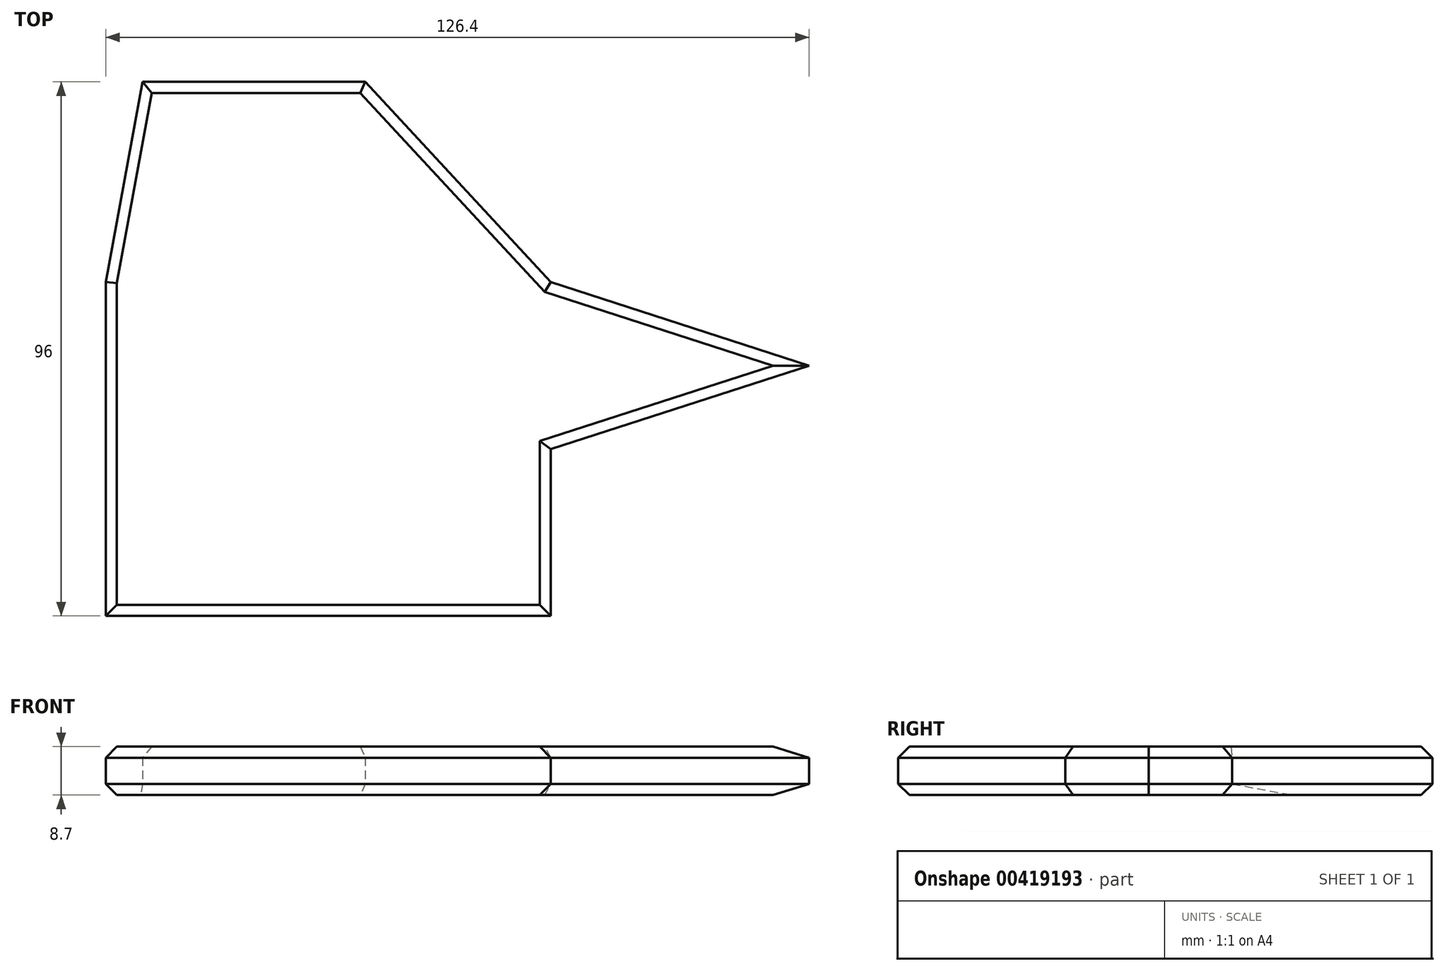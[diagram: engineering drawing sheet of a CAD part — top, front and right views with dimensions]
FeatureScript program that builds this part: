
annotation { "Feature Type Name" : "Feature", "Feature Type Description" : "" }
export const myFeature = defineFeature(function(context is Context, id is Id, definition is map)
    precondition{}
    {
        {
            var Q0;
            Q0=qCreatedBy(makeId("Top.planeOp"),FACE);
            var sketch = newSketch(context, id + "F0", { "sketchPlane" : qUnion([Q0])});
            skLineSegment(sketch, "E0.bottom", {"start": v(-40, 15) * mm, "end": v(40, 15) * mm});
            skLineSegment(sketch, "E0.top", {"start": v(-40, -15) * mm, "end": v(40, -15) * mm});
            skLineSegment(sketch, "E0.left", {"start": v(-40, 15) * mm, "end": v(-40, -15) * mm});
            skLineSegment(sketch, "E0.right", {"start": v(40, 15) * mm, "end": v(40, -15) * mm});
            skPoint(sketch, "E0.middle", {"position": v(0, 0) * mm});
            skLineSegment(sketch, "E1", {"start": v(40, 15) * mm, "end": v(86.4, 0) * mm});
            skLineSegment(sketch, "E2", {"start": v(86.4, 0) * mm, "end": v(40, -15) * mm});
            skLineSegment(sketch, "E3", {"start": v(-40, 15) * mm, "end": v(-33.36, 51) * mm});
            skLineSegment(sketch, "E4", {"start": v(-33.36, 51) * mm, "end": v(6.64, 51) * mm});
            skLineSegment(sketch, "E5", {"start": v(6.64, 51) * mm, "end": v(40, 15) * mm});
            skLineSegment(sketch, "E6.top", {"start": v(-40, -45) * mm, "end": v(40, -45) * mm});
            skLineSegment(sketch, "E6.left", {"start": v(-40, -15) * mm, "end": v(-40, -45) * mm});
            skLineSegment(sketch, "E6.right", {"start": v(40, -15) * mm, "end": v(40, -45) * mm});
            skSolve(sketch);
        }
        {
            var Q0;
            Q0=makeQuery(id+"F0.imprint","IMPRINT",FACE,{"disambiguationData":[TD([[makeQuery(id+"F0.imprint","IMPRINT",EDGE,{"derivedFrom":sQuery(id+"F0.wireOp",EDGE,"E0.bottom")}),1.0]])]});
            var Q1;
            Q1=makeQuery(id+"F0.imprint","IMPRINT",FACE,{"disambiguationData":[TD([[makeQuery(id+"F0.imprint","IMPRINT",EDGE,{"derivedFrom":sQuery(id+"F0.wireOp",EDGE,"E0.right")}),1.0]])]});
            var Q2;
            Q2=makeQuery(id+"F0.imprint","IMPRINT",FACE,{"disambiguationData":[TD([[makeQuery(id+"F0.imprint","IMPRINT",EDGE,{"derivedFrom":sQuery(id+"F0.wireOp",EDGE,"E0.bottom")}),-1.0]])]});
            var Q3;
            Q3=makeQuery(id+"F0.imprint","IMPRINT",FACE,{"disambiguationData":[TD([[makeQuery(id+"F0.imprint","IMPRINT",EDGE,{"derivedFrom":sQuery(id+"F0.wireOp",EDGE,"E0.top")}),-1.0]])]});
            extrude(context, id + "F1", {"entities" : qUnion([Q0, Q1, Q2, Q3]), "endBound" : BoundingType.SYMMETRIC, "depth" : 8.7 * mm});
        }
        {
            var Q0;
            Q0=makeQuery(id+"F1.opExtrude","CAP_EDGE",EDGE,{"disambiguationData":[OSD([sQuery(id+"F0.wireOp",EDGE,"E5")])],"isStart":true});
            var Q1;
            Q1=makeQuery(id+"F1.opExtrude","CAP_EDGE",EDGE,{"disambiguationData":[OSD([sQuery(id+"F0.wireOp",EDGE,"E4")])],"isStart":true});
            var Q2;
            Q2=makeQuery(id+"F1.opExtrude","CAP_EDGE",EDGE,{"disambiguationData":[OSD([sQuery(id+"F0.wireOp",EDGE,"E1")])],"isStart":true});
            var Q3;
            Q3=makeQuery(id+"F1.opExtrude","CAP_EDGE",EDGE,{"disambiguationData":[OSD([sQuery(id+"F0.wireOp",EDGE,"E2")])],"isStart":true});
            var Q4;
            Q4=makeQuery(id+"F1.opExtrude","CAP_EDGE",EDGE,{"disambiguationData":[OSD([sQuery(id+"F0.wireOp",EDGE,"E6.right")])],"isStart":true});
            var Q5;
            Q5=makeQuery(id+"F1.opExtrude","CAP_EDGE",EDGE,{"disambiguationData":[OSD([sQuery(id+"F0.wireOp",EDGE,"E6.top")])],"isStart":true});
            var Q6;
            Q6=makeQuery(id+"F1.opExtrude","CAP_EDGE",EDGE,{"disambiguationData":[OSD([sQuery(id+"F0.wireOp",EDGE,"E0.left"),sQuery(id+"F0.wireOp",EDGE,"E6.left")])],"isStart":true});
            var Q7;
            Q7=makeQuery(id+"F1.opExtrude","CAP_EDGE",EDGE,{"disambiguationData":[OSD([sQuery(id+"F0.wireOp",EDGE,"E4")])],"isStart":false});
            var Q8;
            Q8=makeQuery(id+"F1.opExtrude","CAP_EDGE",EDGE,{"disambiguationData":[OSD([sQuery(id+"F0.wireOp",EDGE,"E5")])],"isStart":false});
            var Q9;
            Q9=makeQuery(id+"F1.opExtrude","CAP_EDGE",EDGE,{"disambiguationData":[OSD([sQuery(id+"F0.wireOp",EDGE,"E1")])],"isStart":false});
            var Q10;
            Q10=makeQuery(id+"F1.opExtrude","CAP_EDGE",EDGE,{"disambiguationData":[OSD([sQuery(id+"F0.wireOp",EDGE,"E2")])],"isStart":false});
            var Q11;
            Q11=makeQuery(id+"F1.opExtrude","CAP_EDGE",EDGE,{"disambiguationData":[OSD([sQuery(id+"F0.wireOp",EDGE,"E6.right")])],"isStart":false});
            var Q12;
            Q12=makeQuery(id+"F1.opExtrude","CAP_EDGE",EDGE,{"disambiguationData":[OSD([sQuery(id+"F0.wireOp",EDGE,"E6.top")])],"isStart":false});
            var Q13;
            Q13=makeQuery(id+"F1.opExtrude","CAP_EDGE",EDGE,{"disambiguationData":[OSD([sQuery(id+"F0.wireOp",EDGE,"E0.left"),sQuery(id+"F0.wireOp",EDGE,"E6.left")])],"isStart":false});
            var Q14;
            Q14=makeQuery(id+"F1.opExtrude","CAP_EDGE",EDGE,{"disambiguationData":[OSD([sQuery(id+"F0.wireOp",EDGE,"E3")])],"isStart":false});
            chamfer(context, id + "F2", {"entities" : qUnion([Q0, Q1, Q2, Q3, Q4, Q5, Q6, Q7, Q8, Q9, Q10, Q11, Q12, Q13, Q14]), "width" : 2 * mm, "tangentPropagation" : true});
        }
    });
